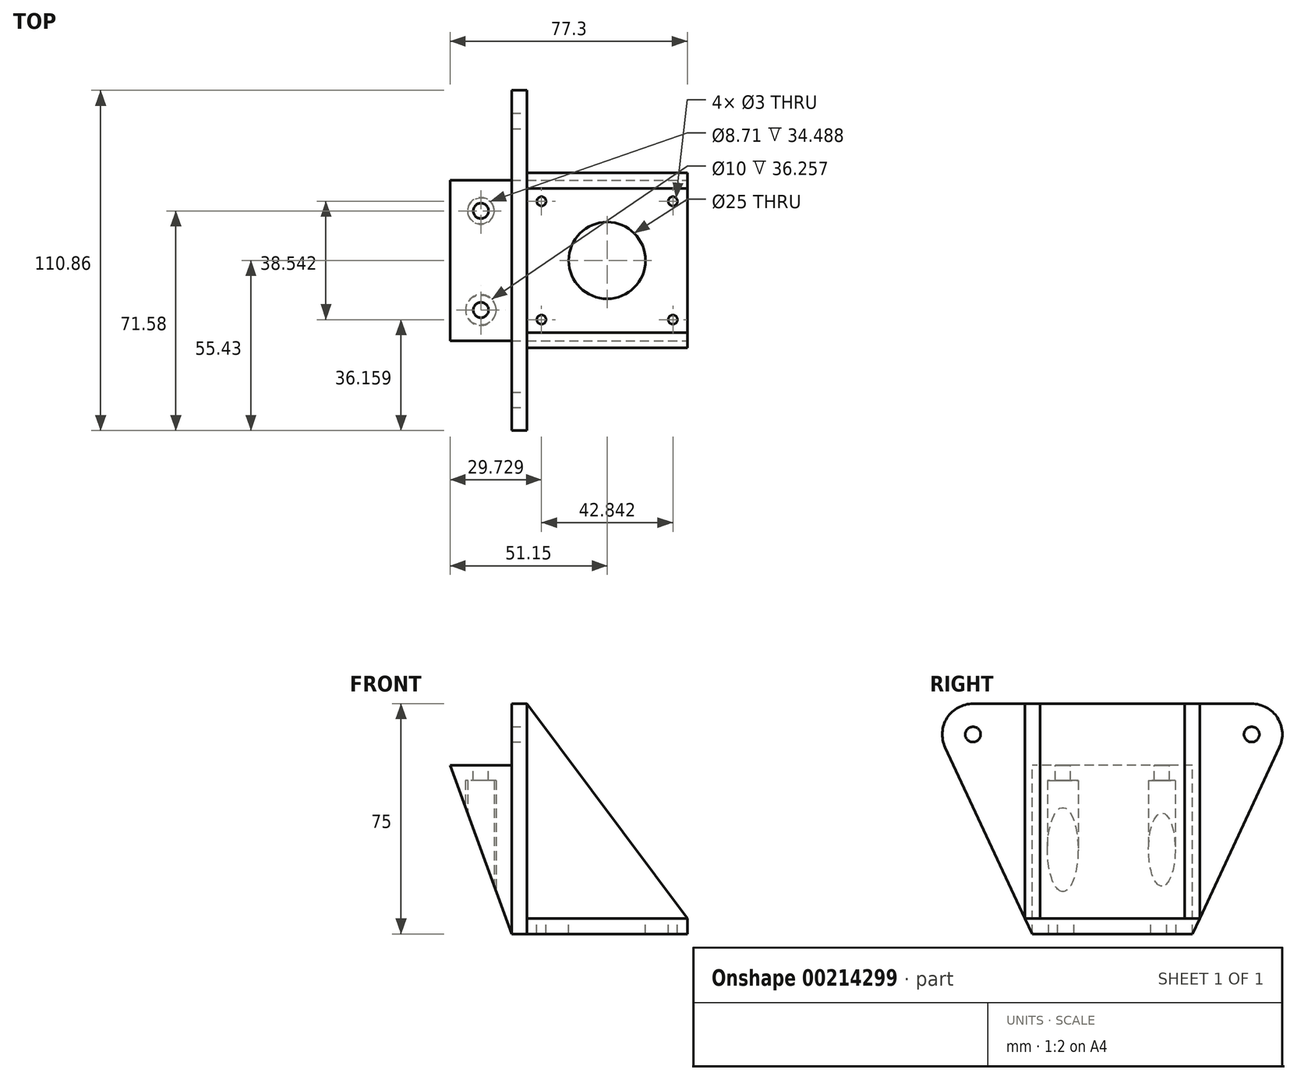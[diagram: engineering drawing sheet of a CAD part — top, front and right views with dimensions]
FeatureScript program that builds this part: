
annotation { "Feature Type Name" : "Feature", "Feature Type Description" : "" }
export const myFeature = defineFeature(function(context is Context, id is Id, definition is map)
    precondition{}
    {
        {
            var Q0;
            Q0=qCreatedBy(makeId("Top.planeOp"),FACE);
            var sketch = newSketch(context, id + "F0", { "sketchPlane" : qUnion([Q0])});
            skLineSegment(sketch, "E0.bottom", {"start": v(0, 0) * mm, "end": v(52.3, 0) * mm});
            skLineSegment(sketch, "E0.top", {"start": v(0, 52.3) * mm, "end": v(52.3, 52.3) * mm});
            skLineSegment(sketch, "E0.left", {"start": v(0, 0) * mm, "end": v(0, 52.3) * mm});
            skLineSegment(sketch, "E0.right", {"start": v(52.3, 0) * mm, "end": v(52.3, 52.3) * mm});
            skSolve(sketch);
        }
        {
            var Q0;
            Q0 = qSketchRegion(id + "F0", true);
            extrude(context, id + "F1", {"entities" : qUnion([Q0]), "depth" : 5 * mm});
        }
        {
            var Q0;
            Q0=qCreatedBy(makeId("Right.planeOp"),FACE);
            var sketch = newSketch(context, id + "F2", { "sketchPlane" : qUnion([Q0])});
            skLineSegment(sketch, "E1.0", {"start": v(52.3, 5) * mm, "end": v(52.3, 0) * mm});
            skLineSegment(sketch, "E2.0", {"start": v(0, 5) * mm, "end": v(52.3, 5) * mm});
            skLineSegment(sketch, "E3.0.0", {"start": v(52.3, 0) * mm, "end": v(0, 0) * mm});
            skLineSegment(sketch, "E4", {"start": v(52.3, 0) * mm, "end": v(87.27, 75) * mm});
            skLineSegment(sketch, "E5", {"start": v(26.15, 0) * mm, "end": v(26.15, 78.02) * mm, "construction": true});
            skLineSegment(sketch, "E6", {"start": v(87.27, 75) * mm, "end": v(26.15, 75) * mm});
            skLineSegment(sketch, "E7.MirrorCS", {"start": v(-34.97, 75) * mm, "end": v(26.15, 75) * mm});
            skLineSegment(sketch, "E8.MirrorCS", {"start": v(0, 0) * mm, "end": v(-34.97, 75) * mm});
            skSolve(sketch);
        }
        {
            var Q0;
            Q0 = qSketchRegion(id + "F2", true);
            extrude(context, id + "F3", {"entities" : qUnion([Q0]), "operationType" : NewBodyOperationType.ADD, "oppositeDirection" : true, "depth" : 5 * mm});
        }
        {
            var Q0;
            Q0=makeQuery(id+"F3.opExtrude","CAP_FACE",FACE,{"disambiguationData":[OSD([sQuery(id+"F2.wireOp",EDGE,"E3.0.0"),sQuery(id+"F2.wireOp",EDGE,"E4"),sQuery(id+"F2.wireOp",EDGE,"E6"),sQuery(id+"F2.wireOp",EDGE,"E7.MirrorCS"),sQuery(id+"F2.wireOp",EDGE,"E8.MirrorCS")])],"isStart":false});
            var sketch = newSketch(context, id + "F4", { "sketchPlane" : qUnion([Q0])});
            skLineSegment(sketch, "E9.bottom", {"start": v(-52.3, 0) * mm, "end": v(0, 0) * mm});
            skLineSegment(sketch, "E9.top", {"start": v(-52.3, 55) * mm, "end": v(0, 55) * mm});
            skLineSegment(sketch, "E9.left", {"start": v(-52.3, 0) * mm, "end": v(-52.3, 55) * mm});
            skLineSegment(sketch, "E9.right", {"start": v(0, 0) * mm, "end": v(0, 55) * mm});
            skSolve(sketch);
        }
        {
            var Q0;
            Q0 = qSketchRegion(id + "F4", true);
            extrude(context, id + "F5", {"entities" : qUnion([Q0]), "operationType" : NewBodyOperationType.ADD, "depth" : 20 * mm});
        }
        {
            var Q0;
            Q0=makeQuery(id+"F5.opExtrude","SWEPT_FACE",FACE,{"disambiguationData":[OSD([sQuery(id+"F4.wireOp",EDGE,"E9.left")])]});
            var sketch = newSketch(context, id + "F6", { "sketchPlane" : qUnion([Q0])});
            skLineSegment(sketch, "E10", {"start": v(5, 0) * mm, "end": v(25, 55) * mm});
            skLineSegment(sketch, "E11", {"start": v(25, 55) * mm, "end": v(25, 0) * mm});
            skLineSegment(sketch, "E12", {"start": v(25, 0) * mm, "end": v(5, 0) * mm});
            skSolve(sketch);
        }
        {
            var Q0;
            Q0 = qSketchRegion(id + "F6", true);
            extrude(context, id + "F7", {"entities" : qUnion([Q0]), "operationType" : NewBodyOperationType.REMOVE, "endBound" : BoundingType.UP_TO_NEXT, "oppositeDirection" : true, "depth" : 25 * mm});
        }
        {
            var Q0;
            Q0=qCreatedBy(makeId("Top.planeOp"),FACE);
            var sketch = newSketch(context, id + "F8", { "sketchPlane" : qUnion([Q0])});
            skCircle(sketch, "E13", {"center": v(-15, 10) * mm, "radius": 5 * mm});
            skCircle(sketch, "E14", {"center": v(-15, 42.3) * mm, "radius": 4.36 * mm});
            skSolve(sketch);
        }
        {
            var Q0;
            Q0 = qSketchRegion(id + "F8", true);
            extrude(context, id + "F9", {"entities" : qUnion([Q0]), "operationType" : NewBodyOperationType.REMOVE, "depth" : 50 * mm});
        }
        {
            var Q0;
            Q0=makeQuery(id+"F5.opExtrude","SWEPT_FACE",FACE,{"disambiguationData":[OSD([sQuery(id+"F4.wireOp",EDGE,"E9.top")])]});
            var sketch = newSketch(context, id + "F10", { "sketchPlane" : qUnion([Q0])});
            skCircle(sketch, "E15.0", {"center": v(-15, 10) * mm, "radius": 5 * mm, "construction": true});
            skCircle(sketch, "E16.0", {"center": v(-15, 42.3) * mm, "radius": 4.36 * mm, "construction": true});
            skCircle(sketch, "E17", {"center": v(-15, 42.3) * mm, "radius": 2.5 * mm});
            skCircle(sketch, "E18", {"center": v(-15, 10) * mm, "radius": 2.5 * mm});
            skSolve(sketch);
        }
        {
            var Q0;
            Q0 = qSketchRegion(id + "F10", true);
            extrude(context, id + "F11", {"entities" : qUnion([Q0]), "operationType" : NewBodyOperationType.REMOVE, "endBound" : BoundingType.THROUGH_ALL, "oppositeDirection" : true, "depth" : 25 * mm});
        }
        {
            var Q0;
            Q0=makeQuery(id+"F1.opExtrude","SWEPT_FACE",FACE,{"disambiguationData":[OSD([sQuery(id+"F0.wireOp",EDGE,"E0.right")])]});
            var sketch = newSketch(context, id + "F12", { "sketchPlane" : qUnion([Q0])});
            skLineSegment(sketch, "E19", {"start": v(0, 5) * mm, "end": v(-2.37, 5) * mm});
            skLineSegment(sketch, "E20", {"start": v(-2.37, 5) * mm, "end": v(0, 0) * mm});
            skLineSegment(sketch, "E21", {"start": v(0, 0) * mm, "end": v(0, 5) * mm});
            skLineSegment(sketch, "E22", {"start": v(52.3, 5) * mm, "end": v(52.3, 0) * mm});
            skLineSegment(sketch, "E23", {"start": v(26.15, 0) * mm, "end": v(26.15, 21.87) * mm, "construction": true});
            skLineSegment(sketch, "E24.MirrorCS", {"start": v(52.3, 0) * mm, "end": v(52.3, 5) * mm});
            skLineSegment(sketch, "E25.MirrorCS", {"start": v(54.67, 5) * mm, "end": v(52.3, 0) * mm});
            skLineSegment(sketch, "E26.MirrorCS", {"start": v(52.3, 5) * mm, "end": v(54.67, 5) * mm});
            skSolve(sketch);
        }
        {
            var Q0;
            Q0 = qSketchRegion(id + "F12", true);
            var Q1;
            Q1=makeQuery(id+"F3.opExtrude","CAP_FACE",FACE,{"disambiguationData":[OSD([sQuery(id+"F2.wireOp",EDGE,"E3.0.0"),sQuery(id+"F2.wireOp",EDGE,"E4"),sQuery(id+"F2.wireOp",EDGE,"E6"),sQuery(id+"F2.wireOp",EDGE,"E7.MirrorCS"),sQuery(id+"F2.wireOp",EDGE,"E8.MirrorCS")])],"isStart":true});
            extrude(context, id + "F13", {"entities" : qUnion([Q0]), "operationType" : NewBodyOperationType.ADD, "endBound" : BoundingType.UP_TO_SURFACE, "oppositeDirection" : true, "endBoundEntityFace" : qUnion([Q1]), "depth" : 25 * mm});
        }
        {
            var Q0;
            Q0=makeQuery(id+"F13.boolean.opBoolean","MERGE",FACE,{"derivedFrom":[makeQuery(id+"F1.opExtrude","CAP_FACE",FACE,{"disambiguationData":[OSD([sQuery(id+"F0.wireOp",EDGE,"E0.bottom"),sQuery(id+"F0.wireOp",EDGE,"E0.top"),sQuery(id+"F0.wireOp",EDGE,"E0.left"),sQuery(id+"F0.wireOp",EDGE,"E0.right")])],"isStart":false}),makeQuery(id+"F13.opExtrude","SWEPT_FACE",FACE,{"disambiguationData":[OSD([sQuery(id+"F12.wireOp",EDGE,"E19")])]}),makeQuery(id+"F13.opExtrude","SWEPT_FACE",FACE,{"disambiguationData":[OSD([sQuery(id+"F12.wireOp",EDGE,"E26.MirrorCS")])]})]});
            var sketch = newSketch(context, id + "F14", { "sketchPlane" : qUnion([Q0])});
            skLineSegment(sketch, "E27.bottom", {"start": v(0, 54.67) * mm, "end": v(52.3, 54.67) * mm});
            skLineSegment(sketch, "E27.top", {"start": v(0, 49.67) * mm, "end": v(52.3, 49.67) * mm});
            skLineSegment(sketch, "E27.left", {"start": v(0, 54.67) * mm, "end": v(0, 49.67) * mm});
            skLineSegment(sketch, "E27.right", {"start": v(52.3, 54.67) * mm, "end": v(52.3, 49.67) * mm});
            skLineSegment(sketch, "E28", {"start": v(52.3, 26.15) * mm, "end": v(-40.93, 26.15) * mm, "construction": true});
            skLineSegment(sketch, "E29.MirrorCS", {"start": v(0, 2.63) * mm, "end": v(52.3, 2.63) * mm});
            skLineSegment(sketch, "E30.MirrorCS", {"start": v(0, -2.37) * mm, "end": v(52.3, -2.37) * mm});
            skLineSegment(sketch, "E31.MirrorCS", {"start": v(52.3, -2.37) * mm, "end": v(52.3, 2.63) * mm});
            skLineSegment(sketch, "E32.MirrorCS", {"start": v(0, -2.37) * mm, "end": v(0, 2.63) * mm});
            skSolve(sketch);
        }
        {
            var Q0;
            Q0 = qSketchRegion(id + "F14", true);
            var Q1;
            Q1=makeQuery(id+"F3.opExtrude","SWEPT_FACE",FACE,{"disambiguationData":[OSD([sQuery(id+"F2.wireOp",EDGE,"E6"),sQuery(id+"F2.wireOp",EDGE,"E7.MirrorCS")])]});
            extrude(context, id + "F15", {"entities" : qUnion([Q0]), "operationType" : NewBodyOperationType.ADD, "endBound" : BoundingType.UP_TO_SURFACE, "endBoundEntityFace" : qUnion([Q1]), "depth" : 25 * mm});
        }
        {
            var Q0;
            Q0=makeQuery(id+"F15.opExtrude","SWEPT_FACE",FACE,{"disambiguationData":[OSD([sQuery(id+"F14.wireOp",EDGE,"E30.MirrorCS")])]});
            var sketch = newSketch(context, id + "F16", { "sketchPlane" : qUnion([Q0])});
            skLineSegment(sketch, "E33", {"start": v(0, 75) * mm, "end": v(52.3, 5) * mm});
            skLineSegment(sketch, "E34", {"start": v(52.3, 5) * mm, "end": v(52.3, 75) * mm});
            skLineSegment(sketch, "E35", {"start": v(52.3, 75) * mm, "end": v(0, 75) * mm});
            skSolve(sketch);
        }
        {
            var Q0;
            Q0 = qSketchRegion(id + "F16", true);
            extrude(context, id + "F17", {"entities" : qUnion([Q0]), "operationType" : NewBodyOperationType.REMOVE, "endBound" : BoundingType.THROUGH_ALL, "oppositeDirection" : true, "depth" : 25 * mm});
        }
        {
            var Q0;
            Q0=makeQuery(id+"F3.opExtrude","SWEPT_EDGE",EDGE,{"disambiguationData":[OSD([sQuery(id+"F2.wireOp",EDGE,"E7.MirrorCS"),sQuery(id+"F2.wireOp",EDGE,"E8.MirrorCS")])]});
            var Q1;
            Q1=makeQuery(id+"F3.opExtrude","SWEPT_EDGE",EDGE,{"disambiguationData":[OSD([sQuery(id+"F2.wireOp",EDGE,"E4"),sQuery(id+"F2.wireOp",EDGE,"E6")])]});
            fillet(context, id + "F18", {"entities" : qUnion([Q0, Q1]), "radius" : 10 * mm, "tangentPropagation" : true, "allowEdgeOverflow" : false});
        }
        {
            var Q0;
            Q0=makeQuery(id+"F13.boolean.opBoolean","MERGE",FACE,{"derivedFrom":[makeQuery(id+"F1.opExtrude","CAP_FACE",FACE,{"disambiguationData":[OSD([sQuery(id+"F0.wireOp",EDGE,"E0.bottom"),sQuery(id+"F0.wireOp",EDGE,"E0.top"),sQuery(id+"F0.wireOp",EDGE,"E0.left"),sQuery(id+"F0.wireOp",EDGE,"E0.right")])],"isStart":false}),makeQuery(id+"F13.opExtrude","SWEPT_FACE",FACE,{"disambiguationData":[OSD([sQuery(id+"F12.wireOp",EDGE,"E19")])]}),makeQuery(id+"F13.opExtrude","SWEPT_FACE",FACE,{"disambiguationData":[OSD([sQuery(id+"F12.wireOp",EDGE,"E26.MirrorCS")])]})]});
            var sketch = newSketch(context, id + "F19", { "sketchPlane" : qUnion([Q0])});
            skLineSegment(sketch, "E36", {"start": v(0, 2.63) * mm, "end": v(52.3, 49.67) * mm, "construction": true});
            skLineSegment(sketch, "E37", {"start": v(52.3, 2.63) * mm, "end": v(0, 49.67) * mm, "construction": true});
            skCircle(sketch, "E38", {"center": v(26.15, 26.15) * mm, "radius": 12.5 * mm});
            skCircle(sketch, "E39", {"center": v(4.73, 6.88) * mm, "radius": 1.5 * mm});
            skCircle(sketch, "E40", {"center": v(4.73, 45.42) * mm, "radius": 1.5 * mm});
            skLineSegment(sketch, "E41", {"start": v(26.15, 26.15) * mm, "end": v(26.15, 72.07) * mm, "construction": true});
            skPoint(sketch, "E41.endSnap0", {"position": v(26.15, 49.67) * mm});
            skLineSegment(sketch, "E42", {"start": v(26.15, 72.07) * mm, "end": v(26.15, 26.15) * mm, "construction": true});
            skLineSegment(sketch, "E43", {"start": v(26.15, -18.68) * mm, "end": v(26.15, 72.07) * mm, "construction": true});
            skCircle(sketch, "E44.MirrorC", {"center": v(47.57, 45.42) * mm, "radius": 1.5 * mm});
            skCircle(sketch, "E45.MirrorC", {"center": v(47.57, 6.88) * mm, "radius": 1.5 * mm});
            skSolve(sketch);
        }
        {
            var Q0;
            Q0 = qSketchRegion(id + "F19", true);
            extrude(context, id + "F20", {"entities" : qUnion([Q0]), "operationType" : NewBodyOperationType.REMOVE, "endBound" : BoundingType.THROUGH_ALL, "oppositeDirection" : true, "depth" : 25 * mm});
        }
        {
            var Q0;
            {var subQ1=sQuery(id+"F2.wireOp",EDGE,"E8.MirrorCS");var subQ2=sQuery(id+"F2.wireOp",EDGE,"E7.MirrorCS");var subQ3=sQuery(id+"F2.wireOp",EDGE,"E6");var subQ4=sQuery(id+"F2.wireOp",EDGE,"E4");var subQ5=sQuery(id+"F2.wireOp",EDGE,"E3.0.0");Q0=makeQuery(id+"F15.boolean.opBoolean","SPLIT",FACE,{"disambiguationData":[TD([makeQuery(id+"F3.opExtrude","SWEPT_FACE",FACE,{"disambiguationData":[OSD([subQ1])]})])],"derivedFrom":makeQuery(id+"F3.opExtrude","CAP_FACE",FACE,{"disambiguationData":[OSD([subQ5,subQ4,subQ3,subQ2,subQ1])],"isStart":true})});}
            var sketch = newSketch(context, id + "F21", { "sketchPlane" : qUnion([Q0])});
            skCircle(sketch, "E46", {"center": v(-19.28, 65) * mm, "radius": 2.5 * mm});
            skCircle(sketch, "E47", {"center": v(71.58, 65) * mm, "radius": 2.5 * mm});
            skSolve(sketch);
        }
        {
            var Q0;
            Q0 = qSketchRegion(id + "F21", true);
            extrude(context, id + "F22", {"entities" : qUnion([Q0]), "operationType" : NewBodyOperationType.REMOVE, "endBound" : BoundingType.THROUGH_ALL, "oppositeDirection" : true, "depth" : 25 * mm});
        }
    });
